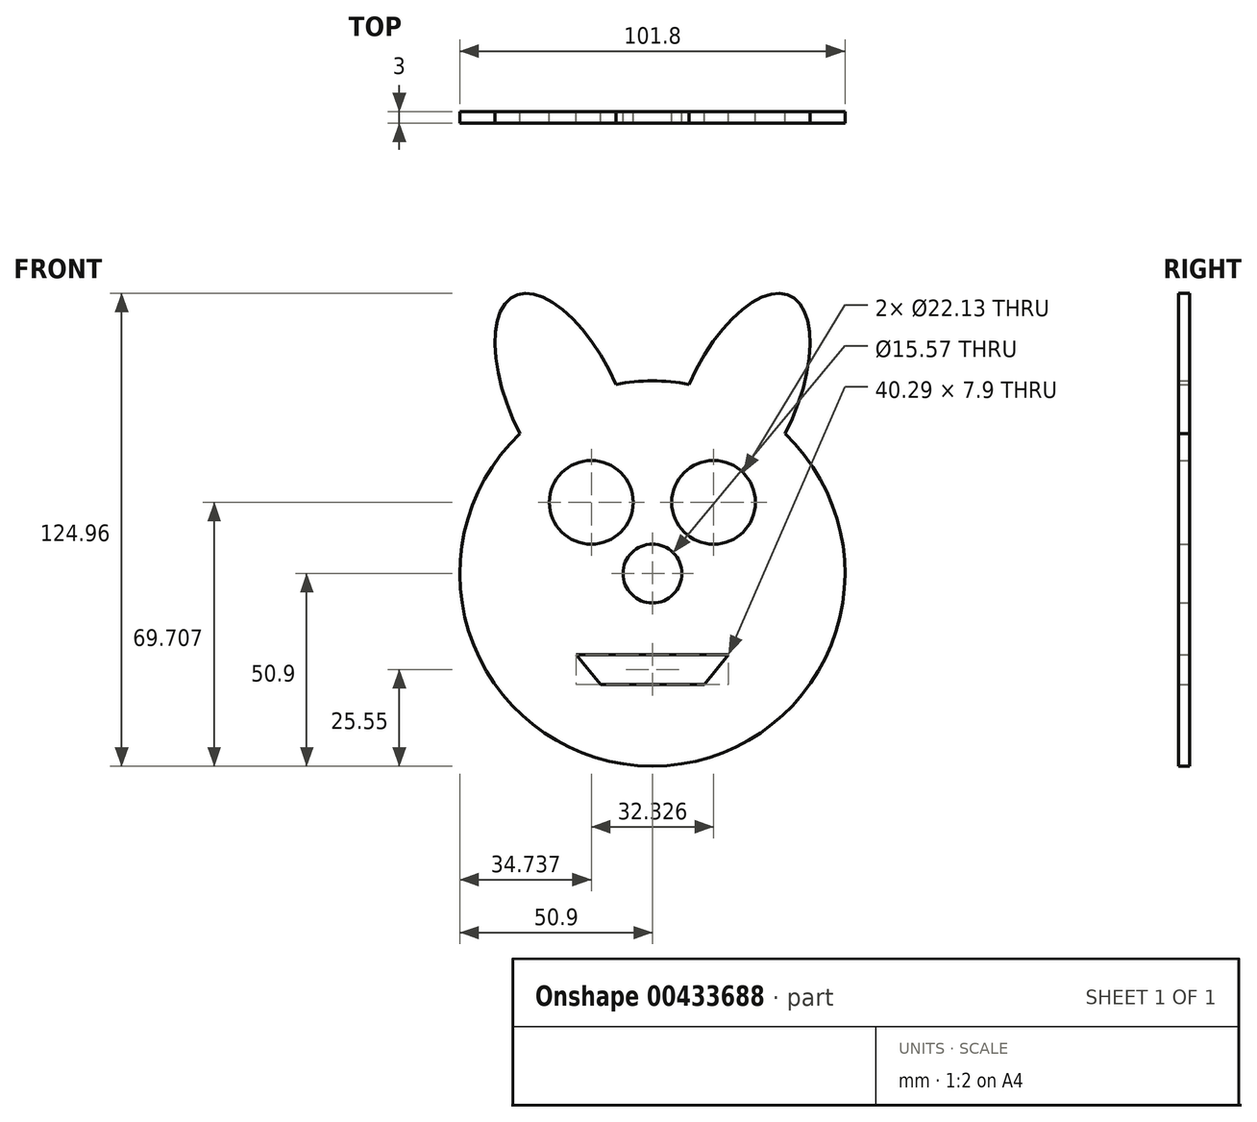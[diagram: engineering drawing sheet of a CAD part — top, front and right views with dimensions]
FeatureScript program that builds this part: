
annotation { "Feature Type Name" : "Feature", "Feature Type Description" : "" }
export const myFeature = defineFeature(function(context is Context, id is Id, definition is map)
    precondition{}
    {
        {
            var Q0;
            Q0=qCreatedBy(makeId("Front.planeOp"),FACE);
            var sketch = newSketch(context, id + "F0", { "sketchPlane" : qUnion([Q0])});
            skArc(sketch, "E0", {"start": v(9.66, 49.97) * mm, "mid": v(0, 50.9) * mm, "end": v(-9.66, 49.97) * mm});
            skCircle(sketch, "E1", {"center": v(-16.16, 18.8) * mm, "radius": 11.06 * mm});
            skArc(sketch, "E2.MirrorC", {"start": v(35.02, 36.93) * mm, "mid": v(0, -50.9) * mm, "end": v(-35.02, 36.93) * mm});
            skCircle(sketch, "E3.MirrorC", {"center": v(16.16, 18.8) * mm, "radius": 11.06 * mm});
            skPoint(sketch, "E4.endSnap0", {"position": v(-7.78, -35.1) * mm});
            skPoint(sketch, "E5.orphan", {"position": v(3.4, -36.84) * mm});
            skPoint(sketch, "E6.orphan", {"position": v(0, -21.4) * mm});
            skPoint(sketch, "E4.end.orphan", {"position": v(5.32, -35.1) * mm});
            skPoint(sketch, "E4.start.orphan", {"position": v(10.86, -36.84) * mm});
            skLineSegment(sketch, "E7", {"start": v(0, -21.4) * mm, "end": v(20.15, -21.4) * mm});
            skLineSegment(sketch, "E8.MirrorCS", {"start": v(0, -21.4) * mm, "end": v(-20.15, -21.4) * mm});
            skLineSegment(sketch, "E9", {"start": v(20.15, -21.4) * mm, "end": v(13.74, -29.3) * mm});
            skLineSegment(sketch, "E10.MirrorCS", {"start": v(-20.15, -21.4) * mm, "end": v(-13.74, -29.3) * mm});
            skLineSegment(sketch, "E11", {"start": v(13.74, -29.3) * mm, "end": v(-13.74, -29.3) * mm});
            skEllipticalArc(sketch, "E12", {});
            skEllipticalArc(sketch, "E13.MirrorC", {});
            skArc(sketch, "E14.trimOffspring", {"start": v(-9.66, 49.97) * mm, "mid": v(0, 50.9) * mm, "end": v(9.66, 49.97) * mm});
            skArc(sketch, "E15.trimOffspring", {"start": v(-35.02, 36.93) * mm, "mid": v(0, -50.9) * mm, "end": v(35.02, 36.93) * mm});
            skCircle(sketch, "E16", {"center": v(0, 0) * mm, "radius": 7.78 * mm});
            const initialGuessF0  = {"E12": [-0.023221514483491905, 0.04529112985781038, 0.4235554616551991, -0.9058701733151673, 0.031043960331700763, 0.014279988820291899, 1.5223745845563172, 4.795404899370814], "E13.MirrorC": [0.023221514483491905, 0.04529112985781038, -0.4235554616551991, -0.9058701733151673, 0.031043960331700763, 0.014279988820291899, 1.487780407808773, 4.760810722623269]};
            skSetInitialGuess(sketch, initialGuessF0);
            skSolve(sketch);
        }
        {
            var Q0;
            Q0 = qSketchRegion(id + "F0", true);
            extrude(context, id + "F1", {"entities" : qUnion([Q0]), "depth" : 3 * mm});
        }
    });
